# Revit family: 13273 Диван «Eco lounge» Хоббика
name_source: partatom
category: Антураж
revit_build: Autodesk Revit 2018 (Build: 20180423_1000(x64)
units: mm (PartAtom-declared; Revit-internal decimal feet)

## family parameters
Всегда вертикально = Да
Источник визуального образа = Геометрия семейства
На основе рабочей плоскости = Нет
Общий = Нет
При загрузке вырезать с полостями = Нет
Точка расчета площади = Нет

## types (2) — shared parameters
URL = https://hobbyka.ru
Артикул товара = Арт 13273
Высота = 710 мм
Группа модели = Мебель для дома и террас
Длина = 1600 мм
Изготовитель = ООО «Хоббика»
Изображение типоразмера = Диван «Eco lounge» Арт 13273.jpg
Материал изделия = Дерево
Цвет отделки = Ангарская сосна
Цвет подушек = Подушка
Ширина = 900 мм

## per-type parameters (varying)
| type | Версия ангарская сосна | Версия лиственница | Описание |
| Версия ангарская сосна | Да | Нет | Диван «Eco lounge». Версия ангарская сосна |
| Версия лиственница | Нет | Да | Диван «Eco lounge». Версия лиственница |
